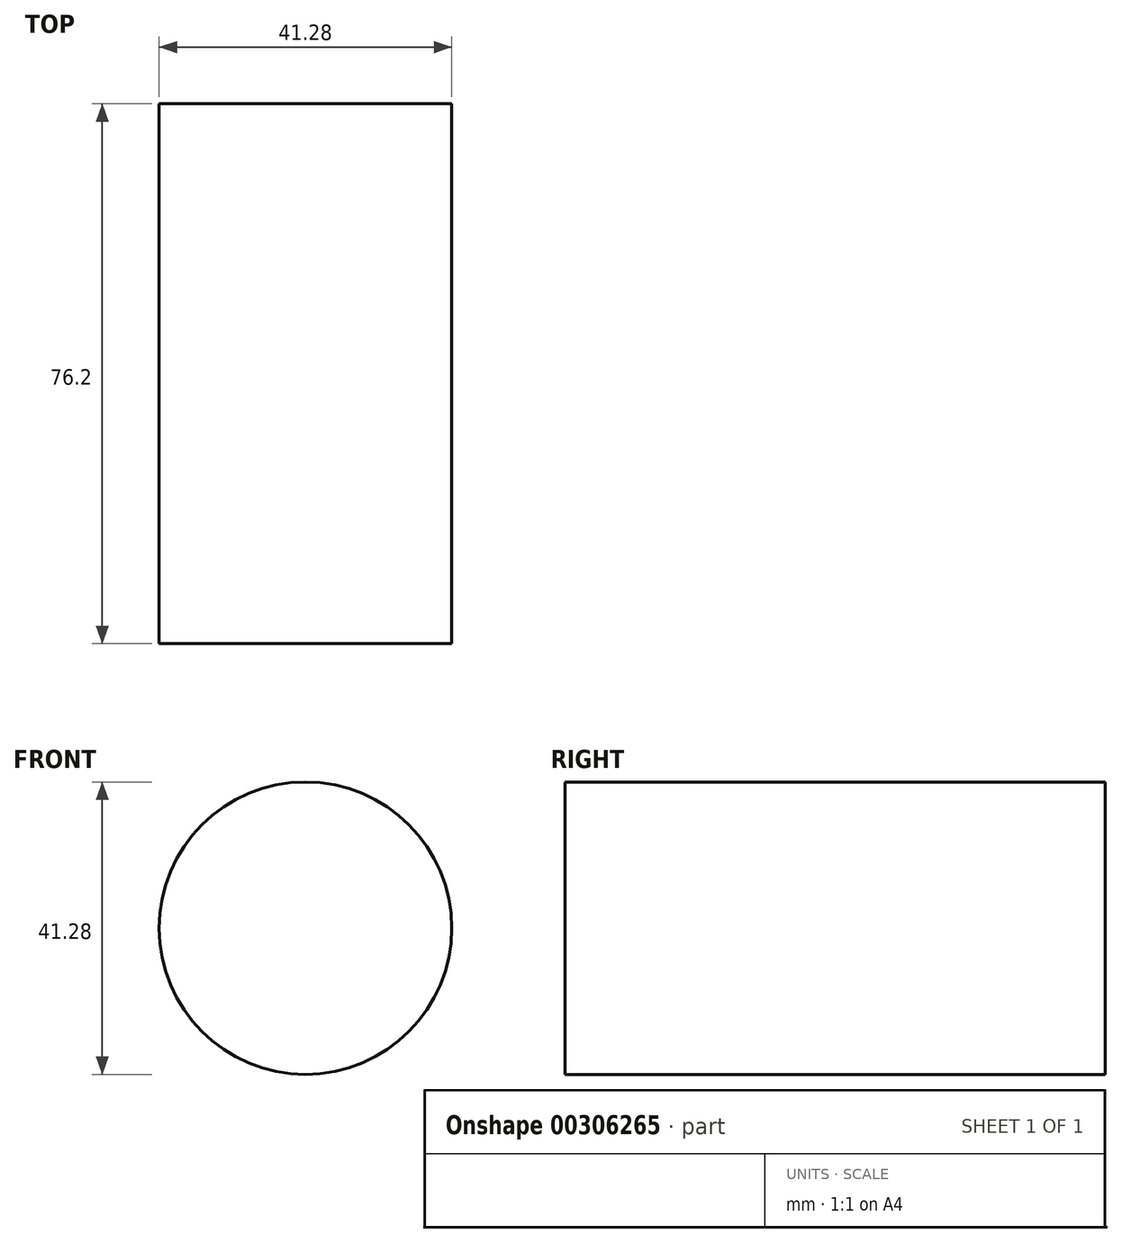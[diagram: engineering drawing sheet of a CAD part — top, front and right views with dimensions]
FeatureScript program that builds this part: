
annotation { "Feature Type Name" : "Feature", "Feature Type Description" : "" }
export const myFeature = defineFeature(function(context is Context, id is Id, definition is map)
    precondition{}
    {
        {
            var Q0;
            Q0=qCreatedBy(makeId("Front.planeOp"),FACE);
            var sketch = newSketch(context, id + "F0", { "sketchPlane" : qUnion([Q0])});
            skCircle(sketch, "E0", {"center": v(0, 0) * mm, "radius": 20.64 * mm});
            skSolve(sketch);
        }
        {
            var Q0;
            Q0 = qSketchRegion(id + "F0", true);
            extrude(context, id + "F1", {"entities" : qUnion([Q0]), "depth" : 76.2 * mm});
        }
    });
